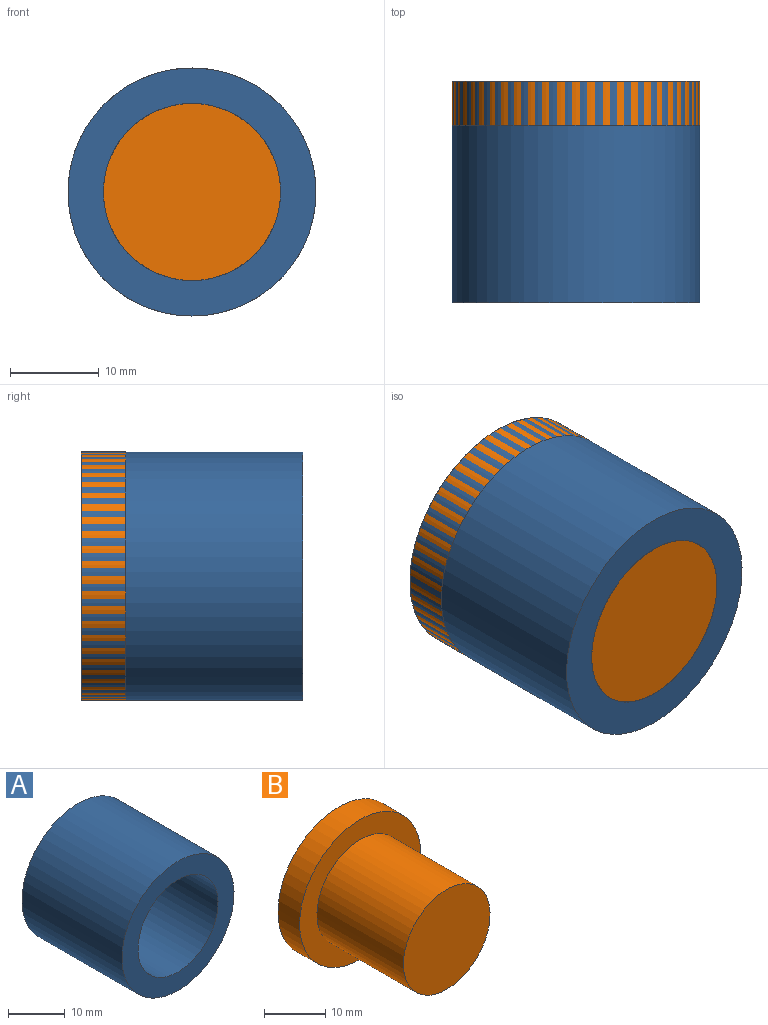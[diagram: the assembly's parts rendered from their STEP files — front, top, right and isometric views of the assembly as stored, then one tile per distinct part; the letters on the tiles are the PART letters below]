
ASSEMBLY  parts=2 mates=1
PART A: 4 faces, bbox 28x25x28 mm
  f0: cylinder r=10mm len=25mm, axis (0,1,0), area 1570.8mm2, adj f2,f3
  f1: cylinder r=14mm len=28mm, axis (0,1,0), area 2199.1mm2, adj f2,f3
  f2: plane 28x28mm, normal (0,-1,0), area 301.6mm2, adj f0,f1
  f3: plane 28x28mm, normal (0,1,0), area 301.6mm2, adj f0,f1
PART B: 5 faces, bbox 28x25x28 mm
  f0: cylinder r=14mm len=28mm, axis (0,1,0), area 439.8mm2, adj f1,f2
  f1: plane 28x28mm, normal (0,-1,0), area 301.6mm2, adj f0,f3
  f2: plane 28x28mm, normal (0,1,0), area 615.8mm2, adj f0
  f3: cylinder r=10mm len=20mm, axis (0,1,0), area 1256.6mm2, adj f1,f4
  f4: plane 20x20mm, normal (0,-1,0), area 314.2mm2, adj f3
PLACE A rot(axis=(0,1,0),0deg) t=(-2.45,3.68,-1)mm
PLACE B rot(axis=(0,1,0),180deg) t=(-2.45,3.68,-1)mm fixed
MATE slider B.f3 <-> A.f0  axis (0,-1,0) through (-2.45,-21.32,-1)mm
